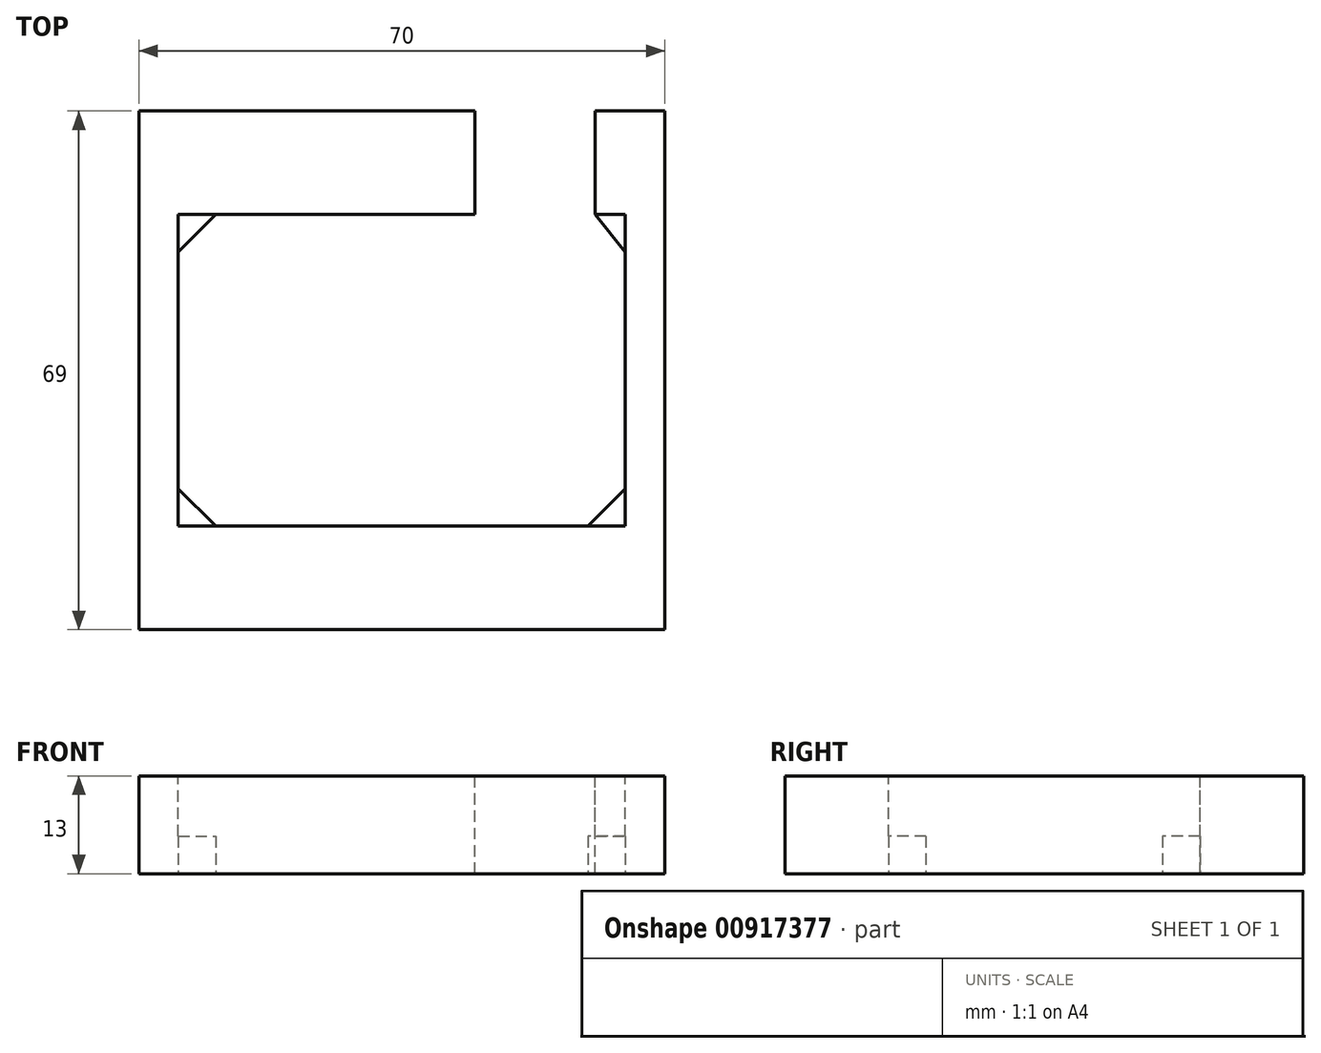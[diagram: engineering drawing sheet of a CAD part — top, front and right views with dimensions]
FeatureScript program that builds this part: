
annotation { "Feature Type Name" : "Feature", "Feature Type Description" : "" }
export const myFeature = defineFeature(function(context is Context, id is Id, definition is map)
    precondition{}
    {
        {
            var Q0;
            Q0=qCreatedBy(makeId("Top.planeOp"),FACE);
            var sketch = newSketch(context, id + "F0", { "sketchPlane" : qUnion([Q0])});
            skLineSegment(sketch, "E0.bottom", {"start": v(-35, 34.5) * mm, "end": v(35, 34.5) * mm});
            skLineSegment(sketch, "E0.top", {"start": v(-35, -34.5) * mm, "end": v(35, -34.5) * mm});
            skLineSegment(sketch, "E0.left", {"start": v(-35, 34.5) * mm, "end": v(-35, -34.5) * mm});
            skLineSegment(sketch, "E0.right", {"start": v(35, 34.5) * mm, "end": v(35, -34.5) * mm});
            skPoint(sketch, "E0.middle", {"position": v(0, 0) * mm});
            skSolve(sketch);
        }
        {
            var Q0;
            Q0=makeQuery(id+"F0.imprint","IMPRINT",FACE,{"disambiguationData":[TD([[makeQuery(id+"F0.imprint","IMPRINT",EDGE,{"derivedFrom":sQuery(id+"F0.wireOp",EDGE,"E0.bottom")}),-1.0]])]});
            extrude(context, id + "F1", {"entities" : qUnion([Q0]), "depth" : 13 * mm, "offsetDistance" : 25 * mm});
        }
        {
            var Q0;
            Q0=makeQuery(id+"F1.opExtrude","CAP_FACE",FACE,{"disambiguationData":[OSD([sQuery(id+"F0.wireOp",EDGE,"E0.bottom"),sQuery(id+"F0.wireOp",EDGE,"E0.top"),sQuery(id+"F0.wireOp",EDGE,"E0.left"),sQuery(id+"F0.wireOp",EDGE,"E0.right")])],"isStart":false});
            var sketch = newSketch(context, id + "F2", { "sketchPlane" : qUnion([Q0])});
            skLineSegment(sketch, "E1.bottom", {"start": v(-29.75, 20.75) * mm, "end": v(29.75, 20.75) * mm});
            skLineSegment(sketch, "E1.top", {"start": v(-29.75, -20.75) * mm, "end": v(29.75, -20.75) * mm});
            skLineSegment(sketch, "E1.left", {"start": v(-29.75, 20.75) * mm, "end": v(-29.75, -20.75) * mm});
            skLineSegment(sketch, "E1.right", {"start": v(29.75, 20.75) * mm, "end": v(29.75, -20.75) * mm});
            skPoint(sketch, "E1.middle", {"position": v(0, 0) * mm});
            skSolve(sketch);
        }
        {
            var Q0;
            Q0 = qSketchRegion(id + "F2", true);
            extrude(context, id + "F3", {"entities" : qUnion([Q0]), "operationType" : NewBodyOperationType.REMOVE, "oppositeDirection" : true, "depth" : 8 * mm, "offsetDistance" : 25 * mm});
        }
        {
            var Q0;
            Q0=makeQuery(id+"F1.opExtrude","CAP_FACE",FACE,{"disambiguationData":[OSD([sQuery(id+"F0.wireOp",EDGE,"E0.bottom"),sQuery(id+"F0.wireOp",EDGE,"E0.top"),sQuery(id+"F0.wireOp",EDGE,"E0.left"),sQuery(id+"F0.wireOp",EDGE,"E0.right")])],"isStart":false});
            var sketch = newSketch(context, id + "F4", { "sketchPlane" : qUnion([Q0])});
            skLineSegment(sketch, "E2", {"start": v(9.75, 20.75) * mm, "end": v(9.75, 34.5) * mm});
            skLineSegment(sketch, "E3", {"start": v(9.75, 34.5) * mm, "end": v(25.75, 34.5) * mm});
            skLineSegment(sketch, "E4", {"start": v(25.75, 34.5) * mm, "end": v(25.75, 20.75) * mm});
            skLineSegment(sketch, "E5", {"start": v(25.75, 20.75) * mm, "end": v(9.75, 20.75) * mm});
            skSolve(sketch);
        }
        {
            var Q0;
            Q0 = qSketchRegion(id + "F4", true);
            extrude(context, id + "F5", {"entities" : qUnion([Q0]), "operationType" : NewBodyOperationType.REMOVE, "endBound" : BoundingType.THROUGH_ALL, "oppositeDirection" : true, "depth" : 25 * mm, "offsetDistance" : 25 * mm});
        }
        {
            var Q0;
            Q0=makeQuery(id+"F1.opExtrude","CAP_FACE",FACE,{"disambiguationData":[OSD([sQuery(id+"F0.wireOp",EDGE,"E0.bottom"),sQuery(id+"F0.wireOp",EDGE,"E0.top"),sQuery(id+"F0.wireOp",EDGE,"E0.left"),sQuery(id+"F0.wireOp",EDGE,"E0.right")])],"isStart":true});
            var sketch = newSketch(context, id + "F6", { "sketchPlane" : qUnion([Q0])});
            skPoint(sketch, "E6", {"position": v(-29.75, -15.75) * mm});
            skPoint(sketch, "E7", {"position": v(-24.75, -20.75) * mm});
            skLineSegment(sketch, "E8", {"start": v(-29.75, -15.75) * mm, "end": v(-24.75, -20.75) * mm});
            skPoint(sketch, "E9", {"position": v(-29.75, 15.75) * mm});
            skPoint(sketch, "E10", {"position": v(-24.75, 20.75) * mm});
            skPoint(sketch, "E11", {"position": v(24.75, 20.75) * mm});
            skPoint(sketch, "E12", {"position": v(29.75, 15.75) * mm});
            skPoint(sketch, "E13", {"position": v(29.75, -15.75) * mm});
            skPoint(sketch, "E14", {"position": v(25.75, -20.75) * mm});
            skLineSegment(sketch, "E15", {"start": v(-29.75, 15.75) * mm, "end": v(-24.75, 20.75) * mm});
            skLineSegment(sketch, "E16", {"start": v(24.75, 20.75) * mm, "end": v(29.75, 15.75) * mm});
            skLineSegment(sketch, "E17", {"start": v(29.75, -15.75) * mm, "end": v(25.75, -20.75) * mm});
            skLineSegment(sketch, "E18", {"start": v(-24.75, -20.75) * mm, "end": v(25.75, -20.75) * mm});
            skLineSegment(sketch, "E19", {"start": v(29.75, 15.75) * mm, "end": v(29.75, -15.75) * mm});
            skLineSegment(sketch, "E20", {"start": v(24.75, 20.75) * mm, "end": v(-24.75, 20.75) * mm});
            skLineSegment(sketch, "E21", {"start": v(-29.75, -15.75) * mm, "end": v(-29.75, 15.75) * mm});
            skSolve(sketch);
        }
        {
            var Q0;
            Q0 = qSketchRegion(id + "F6", true);
            extrude(context, id + "F7", {"entities" : qUnion([Q0]), "operationType" : NewBodyOperationType.REMOVE, "endBound" : BoundingType.THROUGH_ALL, "oppositeDirection" : true, "depth" : 25 * mm, "offsetDistance" : 25 * mm});
        }
    });
